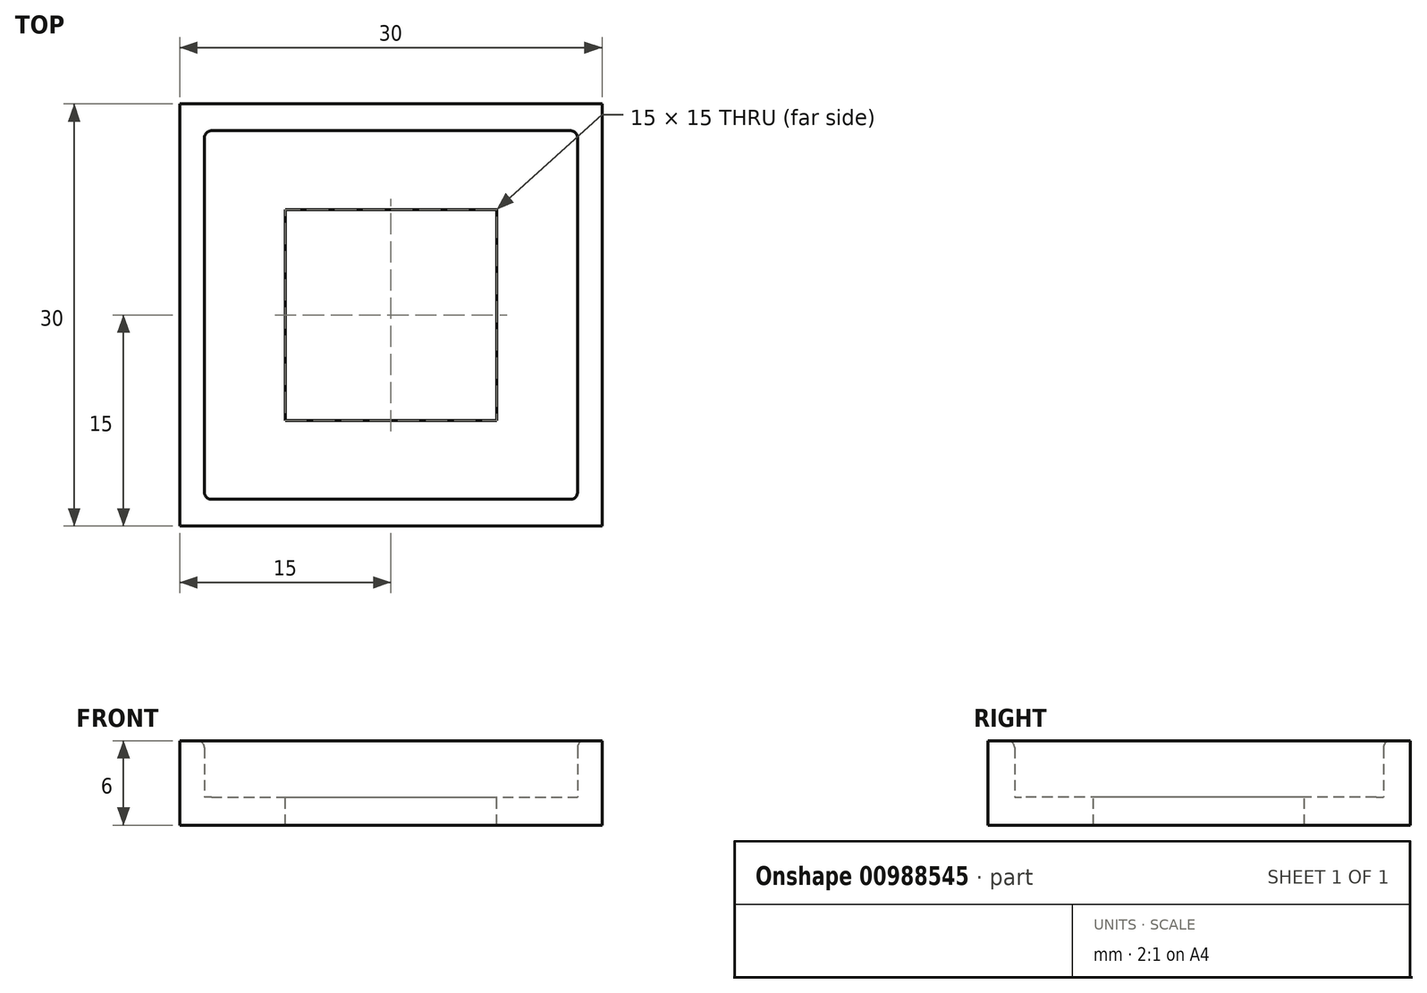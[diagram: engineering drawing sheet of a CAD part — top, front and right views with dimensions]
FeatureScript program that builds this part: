
annotation { "Feature Type Name" : "Feature", "Feature Type Description" : "" }
export const myFeature = defineFeature(function(context is Context, id is Id, definition is map)
    precondition{}
    {
        {
            var Q0;
            Q0=qCreatedBy(makeId("Top.planeOp"),FACE);
            var sketch = newSketch(context, id + "F0", { "sketchPlane" : qUnion([Q0])});
            skLineSegment(sketch, "E0.bottom", {"start": v(-15, 15) * mm, "end": v(15, 15) * mm});
            skLineSegment(sketch, "E0.top", {"start": v(-15, -15) * mm, "end": v(15, -15) * mm});
            skLineSegment(sketch, "E0.left", {"start": v(-15, 15) * mm, "end": v(-15, -15) * mm});
            skLineSegment(sketch, "E0.right", {"start": v(15, 15) * mm, "end": v(15, -15) * mm});
            skPoint(sketch, "E0.middle", {"position": v(0, 0) * mm});
            skLineSegment(sketch, "E1.bottom", {"start": v(-13, 13) * mm, "end": v(13, 13) * mm});
            skLineSegment(sketch, "E1.top", {"start": v(-13, -13) * mm, "end": v(13, -13) * mm});
            skLineSegment(sketch, "E1.left", {"start": v(-13, 13) * mm, "end": v(-13, -13) * mm});
            skLineSegment(sketch, "E1.right", {"start": v(13, 13) * mm, "end": v(13, -13) * mm});
            skSolve(sketch);
        }
        {
            var Q0;
            Q0=makeQuery(id+"F0.imprint","IMPRINT",FACE,{"disambiguationData":[TD([[makeQuery(id+"F0.imprint","IMPRINT",EDGE,{"derivedFrom":sQuery(id+"F0.wireOp",EDGE,"E1.bottom")}),-1.0]])]});
            var Q1;
            Q1=makeQuery(id+"F0.imprint","IMPRINT",FACE,{"disambiguationData":[TD([[makeQuery(id+"F0.imprint","IMPRINT",EDGE,{"derivedFrom":sQuery(id+"F0.wireOp",EDGE,"E0.bottom")}),-1.0]])]});
            extrude(context, id + "F1", {"entities" : qUnion([Q0, Q1]), "depth" : 2 * mm, "offsetDistance" : 25 * mm});
        }
        {
            var Q0;
            Q0=makeQuery(id+"F1.opExtrude","CAP_FACE",FACE,{"disambiguationData":[OSD([sQuery(id+"F0.wireOp",EDGE,"E0.bottom"),sQuery(id+"F0.wireOp",EDGE,"E0.top"),sQuery(id+"F0.wireOp",EDGE,"E0.left"),sQuery(id+"F0.wireOp",EDGE,"E0.right")])],"isStart":false});
            var sketch = newSketch(context, id + "F2", { "sketchPlane" : qUnion([Q0])});
            skLineSegment(sketch, "E2.bottom", {"start": v(-13.25, 13.1) * mm, "end": v(13.25, 13.1) * mm});
            skLineSegment(sketch, "E2.top", {"start": v(-13.25, -13.1) * mm, "end": v(13.25, -13.1) * mm});
            skLineSegment(sketch, "E2.left", {"start": v(-13.25, 13.1) * mm, "end": v(-13.25, -13.1) * mm});
            skLineSegment(sketch, "E2.right", {"start": v(13.25, 13.1) * mm, "end": v(13.25, -13.1) * mm});
            skPoint(sketch, "E2.middle", {"position": v(0, 0) * mm});
            skSolve(sketch);
        }
        {
            var Q0;
            Q0=makeQuery(id+"F2.imprint","IMPRINT",FACE,{"disambiguationData":[TD([[makeQuery(id+"F2.imprint","IMPRINT",EDGE,{"derivedFrom":sQuery(id+"F2.wireOp",EDGE,"E2.bottom")}),1.0]])]});
            extrude(context, id + "F3", {"entities" : qUnion([Q0]), "operationType" : NewBodyOperationType.ADD, "depth" : 4 * mm, "offsetDistance" : 25 * mm});
        }
        {
            var Q0;
            Q0=makeQuery(id+"F3.opExtrude","CAP_EDGE",EDGE,{"disambiguationData":[OSD([sQuery(id+"F2.wireOp",EDGE,"E2.left")])],"isStart":false});
            var Q1;
            Q1=makeQuery(id+"F3.opExtrude","CAP_EDGE",EDGE,{"disambiguationData":[OSD([sQuery(id+"F2.wireOp",EDGE,"E2.bottom")])],"isStart":false});
            var Q2;
            Q2=makeQuery(id+"F3.opExtrude","CAP_EDGE",EDGE,{"disambiguationData":[OSD([sQuery(id+"F2.wireOp",EDGE,"E2.right")])],"isStart":false});
            var Q3;
            Q3=makeQuery(id+"F3.opExtrude","CAP_EDGE",EDGE,{"disambiguationData":[OSD([sQuery(id+"F2.wireOp",EDGE,"E2.top")])],"isStart":false});
            var Q4;
            Q4=makeQuery(id+"F3.opExtrude","SWEPT_EDGE",EDGE,{"disambiguationData":[OSD([sQuery(id+"F2.wireOp",EDGE,"E2.bottom"),sQuery(id+"F2.wireOp",EDGE,"E2.left")])]});
            var Q5;
            Q5=makeQuery(id+"F3.opExtrude","SWEPT_EDGE",EDGE,{"disambiguationData":[OSD([sQuery(id+"F2.wireOp",EDGE,"E2.top"),sQuery(id+"F2.wireOp",EDGE,"E2.left")])]});
            var Q6;
            Q6=makeQuery(id+"F3.opExtrude","SWEPT_EDGE",EDGE,{"disambiguationData":[OSD([sQuery(id+"F2.wireOp",EDGE,"E2.bottom"),sQuery(id+"F2.wireOp",EDGE,"E2.right")])]});
            var Q7;
            Q7=makeQuery(id+"F3.opExtrude","SWEPT_EDGE",EDGE,{"disambiguationData":[OSD([sQuery(id+"F2.wireOp",EDGE,"E2.top"),sQuery(id+"F2.wireOp",EDGE,"E2.right")])]});
            fillet(context, id + "F4", {"entities" : qUnion([Q0, Q1, Q2, Q3, Q4, Q5, Q6, Q7]), "radius" : 0.5 * mm, "tangentPropagation" : true, "allowEdgeOverflow" : false});
        }
        {
            var Q0;
            Q0=makeQuery(id+"F1.opExtrude","CAP_FACE",FACE,{"disambiguationData":[OSD([sQuery(id+"F0.wireOp",EDGE,"E0.bottom"),sQuery(id+"F0.wireOp",EDGE,"E0.top"),sQuery(id+"F0.wireOp",EDGE,"E0.left"),sQuery(id+"F0.wireOp",EDGE,"E0.right")])],"isStart":false});
            var sketch = newSketch(context, id + "F5", { "sketchPlane" : qUnion([Q0])});
            skLineSegment(sketch, "E3.bottom", {"start": v(-7.5, 7.5) * mm, "end": v(7.5, 7.5) * mm});
            skLineSegment(sketch, "E3.top", {"start": v(-7.5, -7.5) * mm, "end": v(7.5, -7.5) * mm});
            skLineSegment(sketch, "E3.left", {"start": v(-7.5, 7.5) * mm, "end": v(-7.5, -7.5) * mm});
            skLineSegment(sketch, "E3.right", {"start": v(7.5, 7.5) * mm, "end": v(7.5, -7.5) * mm});
            skPoint(sketch, "E3.middle", {"position": v(0, 0) * mm});
            skSolve(sketch);
        }
        {
            var Q0;
            Q0=makeQuery(id+"F5.imprint","IMPRINT",FACE,{"disambiguationData":[TD([[makeQuery(id+"F5.imprint","IMPRINT",EDGE,{"derivedFrom":sQuery(id+"F5.wireOp",EDGE,"E3.bottom")}),-1.0]])]});
            extrude(context, id + "F6", {"entities" : qUnion([Q0]), "operationType" : NewBodyOperationType.REMOVE, "oppositeDirection" : true, "depth" : 25 * mm, "offsetDistance" : 25 * mm});
        }
    });
